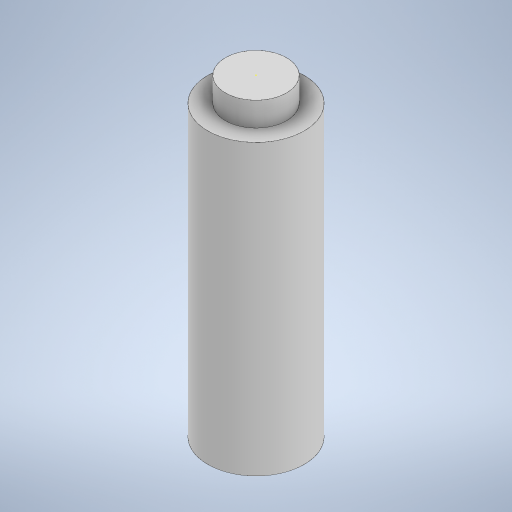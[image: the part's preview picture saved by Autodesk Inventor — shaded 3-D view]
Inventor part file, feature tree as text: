
AUTODESK INVENTOR PART (.ipt)
format: ipt  version: 2024.2 (Build 282272000, 272)  size: 226,816 bytes
history: native  units: mm
features: sketch x3, extrude x2
ambient origin geometry x8: Origin, YZ Plane, XZ Plane, XY Plane, X Axis, Y Axis, Z Axis, Center Point
bodies: Solid1 (feature_tree)
feature tree (5):
  extrude  "Extrusion1"  Depth=60.0mm TaperAngle=0.0deg
  extrude  "Extrusion2"  [1 undecoded]
  sketch  "Sketch3"
  sketch  "Sketch1"  dims[d0=20.0mm d1=60.0mm d2=0.0mm]
  sketch  "Sketch2"  dims[d3=5.0mm d4=0.0mm]
note: 1 required parameter value undecoded (feature->parameter linkage not recoverable at this tier; creation-order binding heuristic only, values carry confidence <= 0.55)
